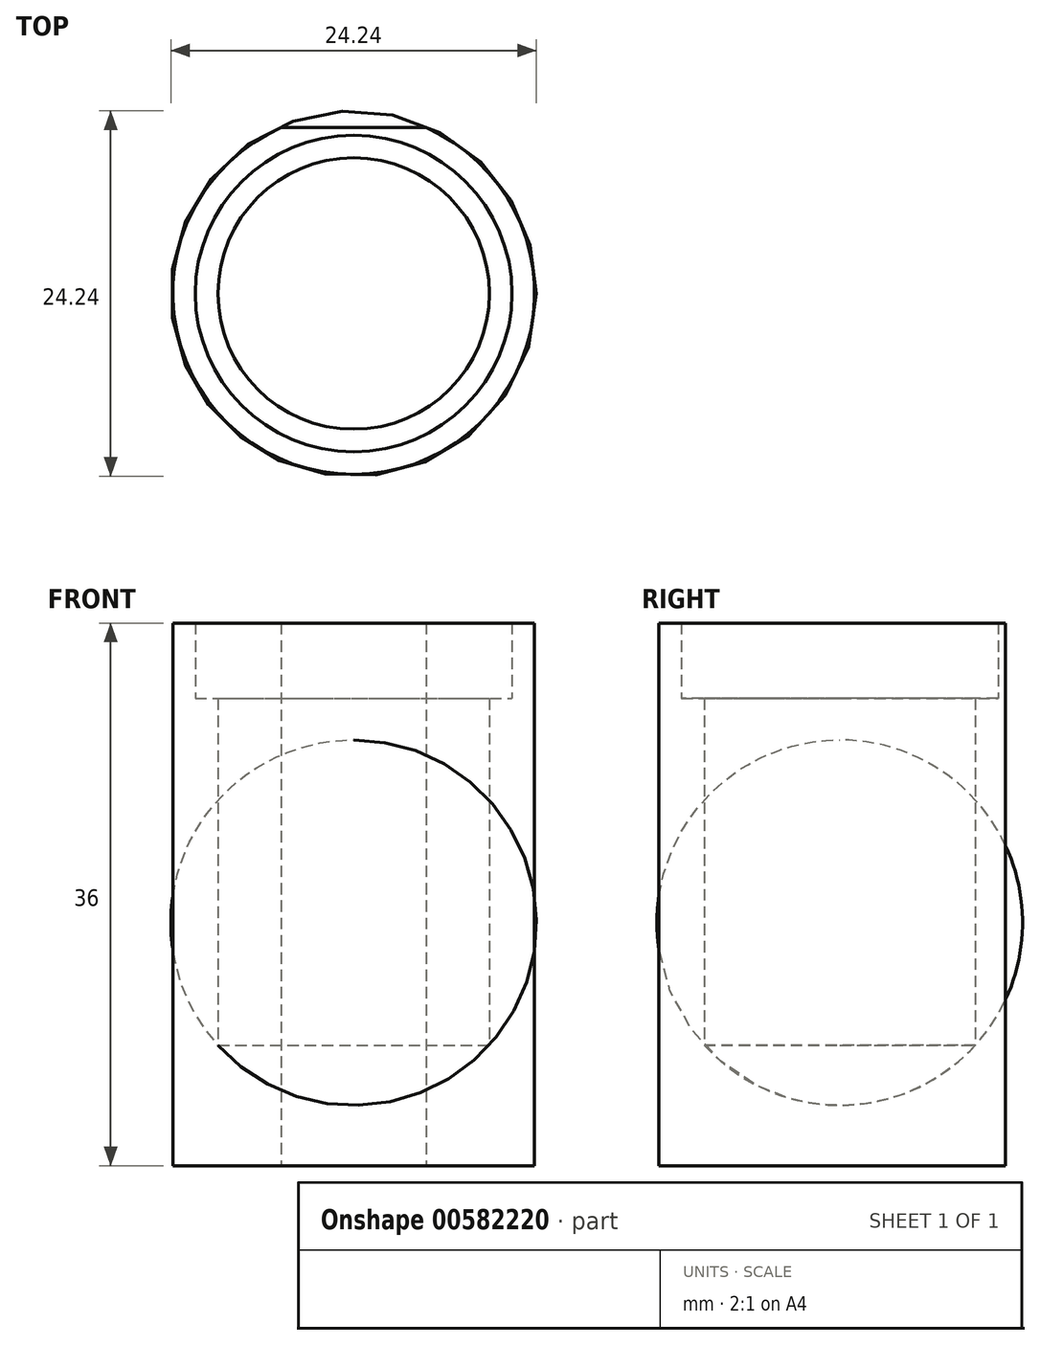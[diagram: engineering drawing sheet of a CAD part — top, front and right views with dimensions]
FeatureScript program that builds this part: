
annotation { "Feature Type Name" : "Feature", "Feature Type Description" : "" }
export const myFeature = defineFeature(function(context is Context, id is Id, definition is map)
    precondition{}
    {
        {
            var Q0;
            Q0=qCreatedBy(makeId("Front.planeOp"),FACE);
            var sketch = newSketch(context, id + "F0", { "sketchPlane" : qUnion([Q0]), "disableImprinting" : false});
            skLineSegment(sketch, "E0.top", {"start": v(12, -4) * mm, "end": v(-12, -4) * mm});
            skLineSegment(sketch, "E0.left", {"start": v(12, 4) * mm, "end": v(12, -4) * mm});
            skLineSegment(sketch, "E0.right", {"start": v(-12, 4) * mm, "end": v(-12, -4) * mm});
            skPoint(sketch, "E0.middle", {"position": v(0, 0) * mm});
            skLineSegment(sketch, "E1.left", {"start": v(-12, 4) * mm, "end": v(-12, 29) * mm});
            skLineSegment(sketch, "E1.right", {"start": v(-9, 4) * mm, "end": v(-9, 27) * mm});
            skLineSegment(sketch, "E2.left", {"start": v(12, 4) * mm, "end": v(12.15, 26.98) * mm});
            skLineSegment(sketch, "E2.right", {"start": v(9, 4) * mm, "end": v(9.15, 27) * mm});
            skLineSegment(sketch, "E3.top", {"start": v(-12, 32) * mm, "end": v(-10.5, 32) * mm});
            skLineSegment(sketch, "E3.left", {"start": v(-12, 29) * mm, "end": v(-12, 32) * mm});
            skLineSegment(sketch, "E3.right", {"start": v(-10.5, 27) * mm, "end": v(-10.5, 32) * mm});
            skArc(sketch, "E4", {"start": v(-9, 4) * mm, "mid": v(0, 0) * mm, "end": v(9, 4) * mm});
            skLineSegment(sketch, "E5", {"start": v(-10.5, 27) * mm, "end": v(-9, 27) * mm});
            skLineSegment(sketch, "E6", {"start": v(0, -4) * mm, "end": v(0, 0) * mm});
            skPoint(sketch, "E7.oppositeSnap0", {"position": v(10.65, 26.99) * mm});
            skLineSegment(sketch, "E7.top", {"start": v(12.15, 32) * mm, "end": v(10.65, 32) * mm});
            skLineSegment(sketch, "E7.left", {"start": v(12.15, 26.98) * mm, "end": v(12.15, 32) * mm});
            skLineSegment(sketch, "E7.right", {"start": v(10.65, 26.98) * mm, "end": v(10.65, 32) * mm});
            skLineSegment(sketch, "E8", {"start": v(9.15, 27) * mm, "end": v(10.65, 26.99) * mm});
            skSolve(sketch);
        }
        {
            var Q0;
            {var subQ1=sQuery(id+"F0.wireOp",EDGE,"E0.right");Q0=makeQuery(id+"F0.imprint","IMPRINT",FACE,{"disambiguationData":[TD([[makeQuery(id+"F0.imprint","IMPRINT",EDGE,{"derivedFrom":subQ1}),1.0]])]});}
            var Q1;
            Q1=sQuery(id+"F0.wireOp",EDGE,"E6");
            revolve(context, id + "F1", {"entities" : qUnion([Q0]), "axis" : qUnion([Q1]), "revolveType" : RevolveType.FULL});
        }
        {
            var Q0;
            Q0=makeQuery(id+"F1.opRevolve","SWEPT_FACE",FACE,{"disambiguationData":[OSD([sQuery(id+"F0.wireOp",EDGE,"E3.top")])]});
            var sketch = newSketch(context, id + "F2", { "sketchPlane" : qUnion([Q0])});
            skLineSegment(sketch, "E9.bottom", {"start": v(0, 11) * mm, "end": v(5, 11) * mm});
            skLineSegment(sketch, "E9.top", {"start": v(0, 12.85) * mm, "end": v(5, 12.85) * mm});
            skLineSegment(sketch, "E9.left", {"start": v(0, 11) * mm, "end": v(0, 12.85) * mm});
            skLineSegment(sketch, "E9.right", {"start": v(5, 11) * mm, "end": v(5, 12.85) * mm});
            skLineSegment(sketch, "E10.MirrorCS", {"start": v(-5, 11) * mm, "end": v(-5, 12.85) * mm});
            skLineSegment(sketch, "E11.MirrorCS", {"start": v(0, 12.85) * mm, "end": v(-5, 12.85) * mm});
            skLineSegment(sketch, "E12.MirrorCS", {"start": v(0, 11) * mm, "end": v(-5, 11) * mm});
            skSolve(sketch);
        }
        {
            var Q0;
            Q0 = qSketchRegion(id + "F2", true);
            extrude(context, id + "F3", {"entities" : qUnion([Q0]), "operationType" : NewBodyOperationType.REMOVE, "oppositeDirection" : true, "depth" : 38 * mm, "offsetDistance" : 25 * mm});
        }
    });
